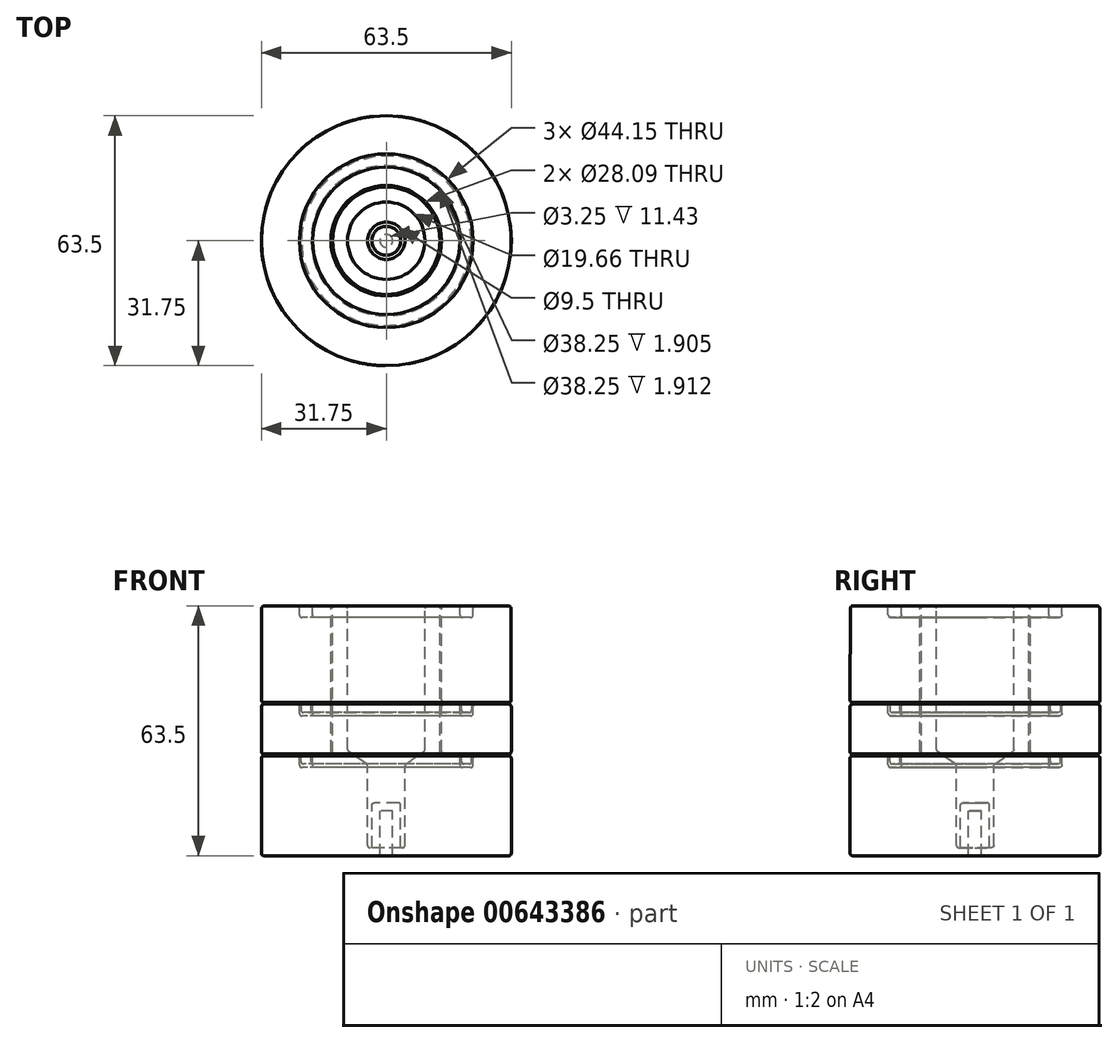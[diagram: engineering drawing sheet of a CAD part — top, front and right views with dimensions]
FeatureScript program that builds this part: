
annotation { "Feature Type Name" : "Feature", "Feature Type Description" : "" }
export const myFeature = defineFeature(function(context is Context, id is Id, definition is map)
    precondition{}
    {
        {
            var Q0;
            Q0=qCreatedBy(makeId("Front.planeOp"),FACE);
            var sketch = newSketch(context, id + "F0", { "sketchPlane" : qUnion([Q0])});
            skLineSegment(sketch, "E0", {"start": v(0, 11.43) * mm, "end": v(1.63, 11.43) * mm});
            skLineSegment(sketch, "E1", {"start": v(1.63, 11.43) * mm, "end": v(1.63, 0) * mm});
            skLineSegment(sketch, "E2", {"start": v(1.63, 0) * mm, "end": v(31.12, 0) * mm});
            skLineSegment(sketch, "E3", {"start": v(31.75, 0.64) * mm, "end": v(31.75, 24.76) * mm});
            skLineSegment(sketch, "E4", {"start": v(13.64, 26) * mm, "end": v(13.64, 62.87) * mm});
            skLineSegment(sketch, "E5", {"start": v(13, 63.5) * mm, "end": v(10.46, 63.5) * mm});
            skLineSegment(sketch, "E6", {"start": v(9.83, 62.87) * mm, "end": v(9.83, 27) * mm});
            skLineSegment(sketch, "E7", {"start": v(4.11, 2.03) * mm, "end": v(3.66, 2.03) * mm});
            skLineSegment(sketch, "E8", {"start": v(3.66, 2.03) * mm, "end": v(3.66, 12.83) * mm});
            skLineSegment(sketch, "E9", {"start": v(3.02, 13.46) * mm, "end": v(0, 13.46) * mm});
            skLineSegment(sketch, "E10", {"start": v(0, 13.46) * mm, "end": v(0, 11.43) * mm});
            skLineSegment(sketch, "E11", {"start": v(14.27, 25.36) * mm, "end": v(18.08, 25.36) * mm});
            skLineSegment(sketch, "E12", {"start": v(18.72, 24.73) * mm, "end": v(18.72, 23.05) * mm});
            skLineSegment(sketch, "E13", {"start": v(19.35, 22.42) * mm, "end": v(21.44, 22.42) * mm});
            skLineSegment(sketch, "E14", {"start": v(22.07, 23.05) * mm, "end": v(22.07, 24.73) * mm});
            skLineSegment(sketch, "E15", {"start": v(22.7, 25.36) * mm, "end": v(31.11, 25.4) * mm});
            skLineSegment(sketch, "E16", {"start": v(9.56, 26.48) * mm, "end": v(5.02, 23.3) * mm});
            skLineSegment(sketch, "E17", {"start": v(4.75, 22.78) * mm, "end": v(4.75, 2.67) * mm});
            skLineSegment(sketch, "E18", {"start": v(14.05, 37.87) * mm, "end": v(14.05, 26.44) * mm});
            skLineSegment(sketch, "E19", {"start": v(14.68, 25.8) * mm, "end": v(19.13, 25.8) * mm});
            skLineSegment(sketch, "E20", {"start": v(19.13, 25.8) * mm, "end": v(19.13, 23.9) * mm});
            skLineSegment(sketch, "E21", {"start": v(19.76, 23.27) * mm, "end": v(21.03, 23.27) * mm});
            skLineSegment(sketch, "E22", {"start": v(21.67, 23.9) * mm, "end": v(21.67, 25.8) * mm});
            skLineSegment(sketch, "E23", {"start": v(21.67, 25.8) * mm, "end": v(31.11, 25.8) * mm});
            skLineSegment(sketch, "E24", {"start": v(31.75, 26.44) * mm, "end": v(31.75, 37.87) * mm});
            skLineSegment(sketch, "E25", {"start": v(14.68, 38.5) * mm, "end": v(18.08, 38.5) * mm});
            skLineSegment(sketch, "E26", {"start": v(18.72, 37.87) * mm, "end": v(18.72, 36.2) * mm});
            skLineSegment(sketch, "E27", {"start": v(19.35, 35.56) * mm, "end": v(21.44, 35.56) * mm});
            skLineSegment(sketch, "E28", {"start": v(22.07, 36.2) * mm, "end": v(22.07, 37.87) * mm});
            skLineSegment(sketch, "E29", {"start": v(22.7, 38.5) * mm, "end": v(31.11, 38.5) * mm});
            skLineSegment(sketch, "E30", {"start": v(14.68, 38.91) * mm, "end": v(19.13, 38.91) * mm});
            skLineSegment(sketch, "E31", {"start": v(19.13, 38.91) * mm, "end": v(19.13, 37) * mm});
            skLineSegment(sketch, "E32", {"start": v(19.76, 36.37) * mm, "end": v(21.03, 36.37) * mm});
            skLineSegment(sketch, "E33", {"start": v(21.66, 37) * mm, "end": v(21.66, 38.91) * mm});
            skLineSegment(sketch, "E34", {"start": v(21.66, 38.91) * mm, "end": v(31.11, 38.91) * mm});
            skLineSegment(sketch, "E35", {"start": v(31.75, 39.55) * mm, "end": v(31.66, 62.87) * mm});
            skLineSegment(sketch, "E36", {"start": v(14.05, 62.87) * mm, "end": v(14.05, 39.55) * mm});
            skPoint(sketch, "E37.visualSharp", {"position": v(31.75, 0) * mm});
            skArc(sketch, "E37.filletArc", {"start": v(31.12, 0) * mm, "mid": v(31.56, 0.19) * mm, "end": v(31.75, 0.64) * mm});
            skPoint(sketch, "E38.visualSharp", {"position": v(31.75, 25.4) * mm});
            skArc(sketch, "E38.filletArc", {"start": v(31.75, 24.76) * mm, "mid": v(31.56, 25.21) * mm, "end": v(31.11, 25.4) * mm});
            skPoint(sketch, "E39.visualSharp", {"position": v(22.07, 25.36) * mm});
            skArc(sketch, "E39.filletArc", {"start": v(22.7, 25.36) * mm, "mid": v(22.26, 25.18) * mm, "end": v(22.07, 24.73) * mm});
            skPoint(sketch, "E40.visualSharp", {"position": v(3.66, 13.46) * mm});
            skArc(sketch, "E40.filletArc", {"start": v(3.66, 12.83) * mm, "mid": v(3.47, 13.28) * mm, "end": v(3.02, 13.46) * mm});
            skPoint(sketch, "E41.visualSharp", {"position": v(4.75, 2.03) * mm});
            skArc(sketch, "E41.filletArc", {"start": v(4.11, 2.03) * mm, "mid": v(4.56, 2.22) * mm, "end": v(4.75, 2.67) * mm});
            skPoint(sketch, "E42.visualSharp", {"position": v(18.72, 25.36) * mm});
            skArc(sketch, "E42.filletArc", {"start": v(18.72, 24.73) * mm, "mid": v(18.53, 25.18) * mm, "end": v(18.08, 25.36) * mm});
            skPoint(sketch, "E43.visualSharp", {"position": v(13.64, 25.36) * mm});
            skArc(sketch, "E43.filletArc", {"start": v(13.64, 26) * mm, "mid": v(13.83, 25.55) * mm, "end": v(14.27, 25.36) * mm});
            skPoint(sketch, "E44.visualSharp", {"position": v(19.13, 23.27) * mm});
            skArc(sketch, "E44.filletArc", {"start": v(19.13, 23.9) * mm, "mid": v(19.31, 23.45) * mm, "end": v(19.76, 23.27) * mm});
            skPoint(sketch, "E45.visualSharp", {"position": v(21.67, 23.27) * mm});
            skArc(sketch, "E45.filletArc", {"start": v(21.03, 23.27) * mm, "mid": v(21.48, 23.45) * mm, "end": v(21.67, 23.9) * mm});
            skPoint(sketch, "E46.visualSharp", {"position": v(14.05, 25.8) * mm});
            skArc(sketch, "E46.filletArc", {"start": v(14.05, 26.44) * mm, "mid": v(14.23, 26) * mm, "end": v(14.68, 25.8) * mm});
            skPoint(sketch, "E47.visualSharp", {"position": v(31.75, 25.8) * mm});
            skArc(sketch, "E47.filletArc", {"start": v(31.11, 25.8) * mm, "mid": v(31.56, 26) * mm, "end": v(31.75, 26.44) * mm});
            skPoint(sketch, "E48.visualSharp", {"position": v(31.75, 38.5) * mm});
            skArc(sketch, "E48.filletArc", {"start": v(31.75, 37.87) * mm, "mid": v(31.56, 38.32) * mm, "end": v(31.11, 38.5) * mm});
            skPoint(sketch, "E49.visualSharp", {"position": v(22.07, 38.5) * mm});
            skArc(sketch, "E49.filletArc", {"start": v(22.7, 38.5) * mm, "mid": v(22.26, 38.32) * mm, "end": v(22.07, 37.87) * mm});
            skPoint(sketch, "E50.visualSharp", {"position": v(18.72, 38.5) * mm});
            skArc(sketch, "E50.filletArc", {"start": v(18.72, 37.87) * mm, "mid": v(18.53, 38.32) * mm, "end": v(18.08, 38.5) * mm});
            skPoint(sketch, "E51.visualSharp", {"position": v(19.13, 36.36) * mm});
            skArc(sketch, "E51.filletArc", {"start": v(19.13, 37) * mm, "mid": v(19.31, 36.55) * mm, "end": v(19.76, 36.37) * mm});
            skPoint(sketch, "E52.visualSharp", {"position": v(21.67, 36.37) * mm});
            skArc(sketch, "E52.filletArc", {"start": v(21.03, 36.37) * mm, "mid": v(21.48, 36.56) * mm, "end": v(21.66, 37) * mm});
            skPoint(sketch, "E53.visualSharp", {"position": v(14.05, 38.5) * mm});
            skArc(sketch, "E53.filletArc", {"start": v(14.68, 38.5) * mm, "mid": v(14.23, 38.32) * mm, "end": v(14.05, 37.87) * mm});
            skPoint(sketch, "E54.visualSharp", {"position": v(14.05, 38.91) * mm});
            skArc(sketch, "E54.filletArc", {"start": v(14.05, 39.55) * mm, "mid": v(14.23, 39.1) * mm, "end": v(14.68, 38.91) * mm});
            skPoint(sketch, "E55.visualSharp", {"position": v(31.75, 38.91) * mm});
            skArc(sketch, "E55.filletArc", {"start": v(31.11, 38.91) * mm, "mid": v(31.56, 39.1) * mm, "end": v(31.75, 39.55) * mm});
            skPoint(sketch, "E56.visualSharp", {"position": v(31.65, 63.5) * mm});
            skArc(sketch, "E56.filletArc", {"start": v(31.66, 62.87) * mm, "mid": v(31.47, 63.31) * mm, "end": v(31.02, 63.5) * mm});
            skPoint(sketch, "E57.visualSharp", {"position": v(14.05, 63.5) * mm});
            skArc(sketch, "E57.filletArc", {"start": v(14.68, 63.5) * mm, "mid": v(14.23, 63.31) * mm, "end": v(14.05, 62.87) * mm});
            skPoint(sketch, "E58.visualSharp", {"position": v(13.64, 63.5) * mm});
            skArc(sketch, "E58.filletArc", {"start": v(13.64, 62.87) * mm, "mid": v(13.45, 63.31) * mm, "end": v(13, 63.5) * mm});
            skPoint(sketch, "E59.visualSharp", {"position": v(9.83, 63.5) * mm});
            skArc(sketch, "E59.filletArc", {"start": v(10.46, 63.5) * mm, "mid": v(10.02, 63.31) * mm, "end": v(9.83, 62.87) * mm});
            skPoint(sketch, "E60.visualSharp", {"position": v(9.83, 26.67) * mm});
            skArc(sketch, "E60.filletArc", {"start": v(9.56, 26.48) * mm, "mid": v(9.76, 26.7) * mm, "end": v(9.83, 27) * mm});
            skPoint(sketch, "E61.visualSharp", {"position": v(4.75, 23.11) * mm});
            skArc(sketch, "E61.filletArc", {"start": v(5.02, 23.3) * mm, "mid": v(4.82, 23.08) * mm, "end": v(4.75, 22.78) * mm});
            skPoint(sketch, "E62.visualSharp", {"position": v(22.07, 22.42) * mm});
            skArc(sketch, "E62.filletArc", {"start": v(21.44, 22.42) * mm, "mid": v(21.89, 22.6) * mm, "end": v(22.07, 23.05) * mm});
            skPoint(sketch, "E63.visualSharp", {"position": v(18.72, 22.42) * mm});
            skArc(sketch, "E63.filletArc", {"start": v(18.72, 23.05) * mm, "mid": v(18.9, 22.6) * mm, "end": v(19.35, 22.42) * mm});
            skPoint(sketch, "E64.visualSharp", {"position": v(18.72, 35.56) * mm});
            skArc(sketch, "E64.filletArc", {"start": v(18.72, 36.2) * mm, "mid": v(18.9, 35.75) * mm, "end": v(19.35, 35.56) * mm});
            skPoint(sketch, "E65.visualSharp", {"position": v(22.07, 35.56) * mm});
            skArc(sketch, "E65.filletArc", {"start": v(21.44, 35.56) * mm, "mid": v(21.89, 35.75) * mm, "end": v(22.07, 36.2) * mm});
            skLineSegment(sketch, "E66", {"start": v(14.68, 63.5) * mm, "end": v(18.08, 63.5) * mm});
            skLineSegment(sketch, "E67", {"start": v(18.72, 62.87) * mm, "end": v(18.72, 61.19) * mm});
            skLineSegment(sketch, "E68", {"start": v(19.35, 60.55) * mm, "end": v(21.44, 60.55) * mm});
            skPoint(sketch, "E68.endSnap0", {"position": v(22.07, 37.03) * mm});
            skLineSegment(sketch, "E69", {"start": v(22.07, 61.19) * mm, "end": v(22.07, 62.87) * mm});
            skLineSegment(sketch, "E70", {"start": v(22.7, 63.5) * mm, "end": v(31.02, 63.5) * mm});
            skPoint(sketch, "E71.visualSharp", {"position": v(18.72, 60.55) * mm});
            skArc(sketch, "E71.filletArc", {"start": v(18.72, 61.19) * mm, "mid": v(18.9, 60.74) * mm, "end": v(19.35, 60.55) * mm});
            skPoint(sketch, "E72.visualSharp", {"position": v(22.07, 60.55) * mm});
            skArc(sketch, "E72.filletArc", {"start": v(21.44, 60.55) * mm, "mid": v(21.89, 60.74) * mm, "end": v(22.07, 61.19) * mm});
            skPoint(sketch, "E73.visualSharp", {"position": v(22.07, 63.5) * mm});
            skArc(sketch, "E73.filletArc", {"start": v(22.7, 63.5) * mm, "mid": v(22.26, 63.31) * mm, "end": v(22.07, 62.87) * mm});
            skPoint(sketch, "E74.visualSharp", {"position": v(18.72, 63.5) * mm});
            skArc(sketch, "E74.filletArc", {"start": v(18.72, 62.87) * mm, "mid": v(18.53, 63.31) * mm, "end": v(18.08, 63.5) * mm});
            skSolve(sketch);
        }
        {
            var Q0;
            Q0=makeQuery(id+"F0.imprint","IMPRINT",FACE,{"disambiguationData":[TD([[makeQuery(id+"F0.imprint","IMPRINT",EDGE,{"derivedFrom":sQuery(id+"F0.wireOp",EDGE,"E0")}),1.0]])]});
            var Q1;
            Q1=makeQuery(id+"F0.imprint","IMPRINT",FACE,{"disambiguationData":[TD([[makeQuery(id+"F0.imprint","IMPRINT",EDGE,{"derivedFrom":sQuery(id+"F0.wireOp",EDGE,"E18")}),1.0]])]});
            var Q2;
            Q2=makeQuery(id+"F0.imprint","IMPRINT",FACE,{"disambiguationData":[TD([[makeQuery(id+"F0.imprint","IMPRINT",EDGE,{"derivedFrom":sQuery(id+"F0.wireOp",EDGE,"E30")}),1.0]])]});
            var Q3;
            Q3=sQuery(id+"F0.wireOp",EDGE,"E10");
            revolve(context, id + "F1", {"entities" : qUnion([Q0, Q1, Q2]), "axis" : qUnion([Q3]), "revolveType" : RevolveType.FULL});
        }
    });
